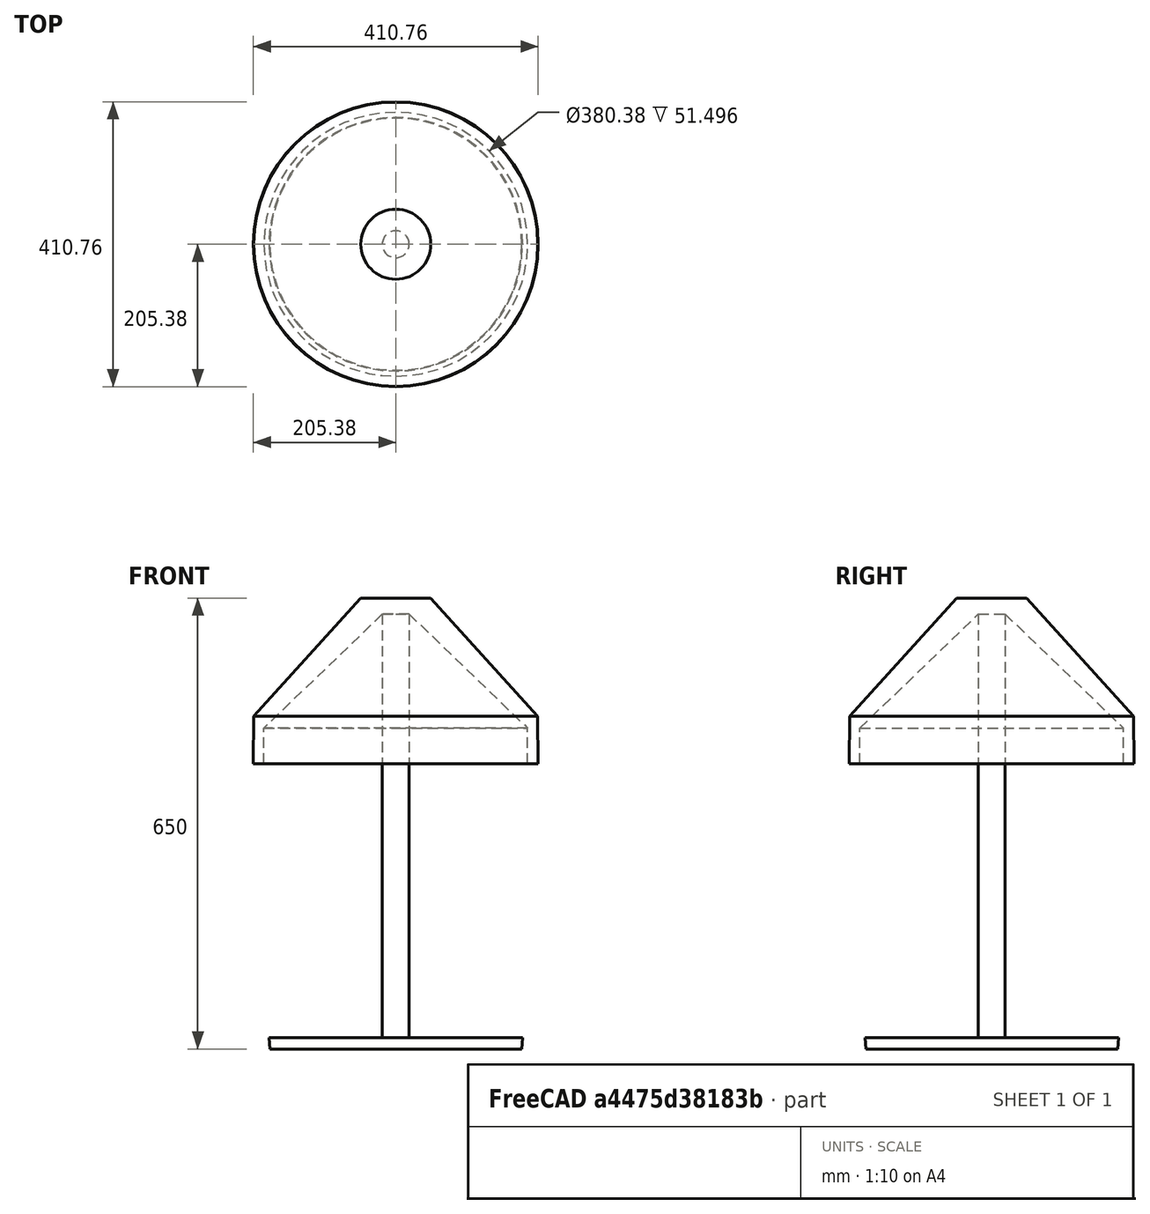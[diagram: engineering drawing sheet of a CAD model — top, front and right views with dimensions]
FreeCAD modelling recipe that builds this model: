
FCSTD DOCUMENT  (FreeCAD 1.0R39319 (Git))
Label: table-lamp
License: All rights reserved
LicenseURL: https://en.wikipedia.org/wiki/All_rights_reserved
objects: Sketcher::SketchObject×1, PartDesign::Revolution×1, PartDesign::Body×1
note: 6 computed .brp shape members not serialized (recipe doc carries the construction recipe); baked Part::Feature solids carry a one-line shape summary decoded from their .brp

FEATURE [Sketcher::SketchObject] Sketch
  ArcFitTolerance = 1e-06
  AttachmentSupport = -> [YZ_Plane]
  FullyConstrained = false
  MakeInternals = false
  MapMode = 5
  Placement = pos=(0,0,0) rot=(0.57735,0.57735,0.57735;2.0944rad)
  sketch-geometry (11):
    g0: LineSegment StartX=0 StartY=0 StartZ=0 EndX=0 EndY=650 EndZ=0
    g1: LineSegment StartX=0 StartY=650 StartZ=0 EndX=-50.5221 EndY=650 EndZ=0
    g2: LineSegment StartX=-50.5221 StartY=650 StartZ=0 EndX=-204.839 EndY=479.859 EndZ=0
    g3: LineSegment StartX=-204.839 StartY=479.859 StartZ=0 EndX=-205.38 EndY=411.198 EndZ=0
    g4: LineSegment StartX=-205.38 StartY=411.198 StartZ=0 EndX=-190.189 EndY=411.198 EndZ=0
    g5: LineSegment StartX=-190.189 StartY=411.198 StartZ=0 EndX=-190.189 EndY=462.694 EndZ=0
    g6: LineSegment StartX=-190.189 StartY=462.694 StartZ=0 EndX=-19.4382 EndY=626.926 EndZ=0
    g7: LineSegment StartX=-19.4382 StartY=626.926 StartZ=0 EndX=-19.4382 EndY=16.2308 EndZ=0
    g8: LineSegment StartX=-19.4382 StartY=16.2308 StartZ=0 EndX=-182.848 EndY=16.2308 EndZ=0
    g9: LineSegment StartX=-182.848 StartY=16.2308 StartZ=0 EndX=-181.745 EndY=-6e-16 EndZ=0
    g10: LineSegment StartX=-181.745 StartY=-6e-16 StartZ=0 EndX=0 EndY=0 EndZ=0
  constraints (20):
    c: Distance(g0) = 650
    c: Coincident(g0,g-1)
    c: PointOnObject(g0,g-2)
    c: Coincident(g1,g0)
    c: Horizontal(g1)
    c: Coincident(g2,g1)
    c: Coincident(g3,g2)
    c: Coincident(g4,g3)
    c: Horizontal(g4)
    c: Coincident(g5,g4)
    c: Vertical(g5)
    c: Coincident(g6,g5)
    c: Coincident(g7,g6)
    c: Vertical(g7)
    c: Coincident(g8,g7)
    c: Horizontal(g8)
    c: Coincident(g9,g8)
    c: PointOnObject(g9,g-1)
    c: Coincident(g10,g9)
    c: Coincident(g10,g0)
FEATURE [PartDesign::Revolution] Revolution
  Angle = 360
  Angle2 = 60
  Axis = (0,0,1)
  Base = (0,0,0)
  Placement = pos=(0,0,0) rot=(1,1,1;2.0944rad)
  Profile = -> Sketch
  ReferenceAxis = -> Sketch [V_Axis]
  Refine = true
  Suppressed = false
  Type = 0
FEATURE [PartDesign::Body] Body
  AllowCompound = false
  Group = -> [Sketch,Revolution]
  Origin = -> Origin
  Tip = -> Revolution
